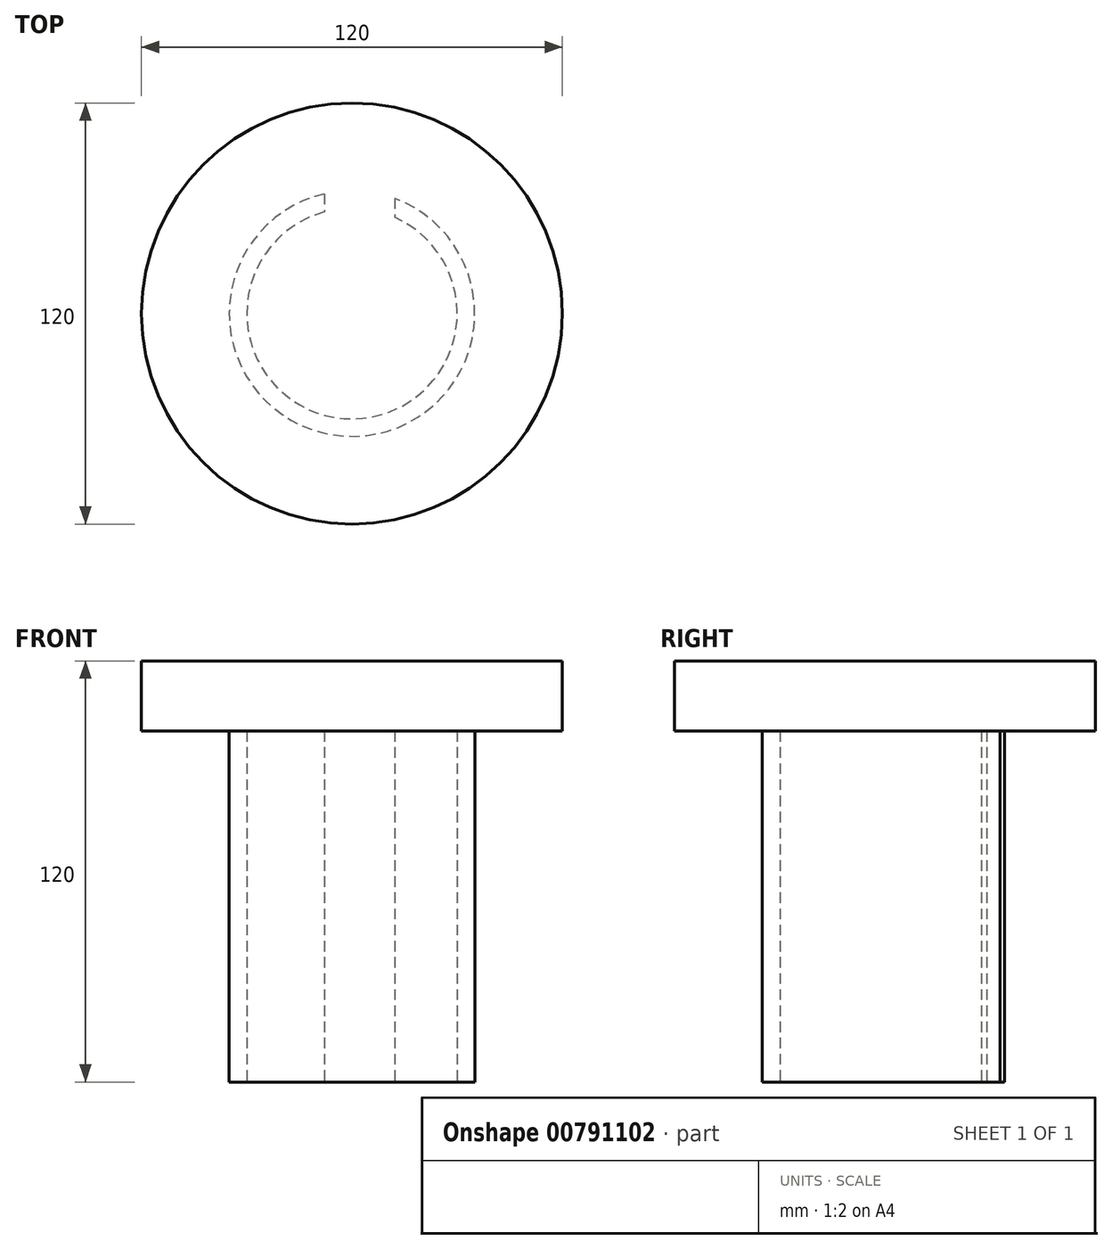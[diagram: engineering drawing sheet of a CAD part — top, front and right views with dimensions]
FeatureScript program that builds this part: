
annotation { "Feature Type Name" : "Feature", "Feature Type Description" : "" }
export const myFeature = defineFeature(function(context is Context, id is Id, definition is map)
    precondition{}
    {
        {
            var Q0;
            Q0=qCreatedBy(makeId("Top.planeOp"),FACE);
            var sketch = newSketch(context, id + "F0", { "sketchPlane" : qUnion([Q0])});
            skCircle(sketch, "E0", {"center": v(0, 0) * mm, "radius": 60 * mm});
            skSolve(sketch);
        }
        {
            var Q0;
            Q0=makeQuery(id+"F0.imprint","IMPRINT",FACE,{"disambiguationData":[TD([[makeQuery(id+"F0.imprint","IMPRINT",EDGE,{"derivedFrom":sQuery(id+"F0.wireOp",EDGE,"E0")}),1.0]])]});
            extrude(context, id + "F1", {"entities" : qUnion([Q0]), "depth" : 20 * mm, "offsetDistance" : 25.4 * mm});
        }
        {
            var Q0;
            Q0=makeQuery(id+"F1.opExtrude","CAP_FACE",FACE,{"disambiguationData":[OSD([sQuery(id+"F0.wireOp",EDGE,"E0")])],"isStart":true});
            var sketch = newSketch(context, id + "F2", { "sketchPlane" : qUnion([Q0])});
            skCircle(sketch, "E1", {"center": v(0, 0) * mm, "radius": 35 * mm});
            skSolve(sketch);
        }
        {
            var Q0;
            Q0 = qSketchRegion(id + "F2", true);
            extrude(context, id + "F3", {"entities" : qUnion([Q0]), "operationType" : NewBodyOperationType.ADD, "depth" : 100 * mm, "offsetDistance" : 25.4 * mm});
        }
        {
            var Q0;
            Q0=makeQuery(id+"F3.opExtrude","CAP_FACE",FACE,{"disambiguationData":[OSD([sQuery(id+"F2.wireOp",EDGE,"E1")])],"isStart":false});
            var sketch = newSketch(context, id + "F4", { "sketchPlane" : qUnion([Q0])});
            skCircle(sketch, "E2", {"center": v(0, 0) * mm, "radius": 30 * mm});
            skLineSegment(sketch, "E3.bottom", {"start": v(12.15, -40.92) * mm, "end": v(-7.85, -40.92) * mm});
            skLineSegment(sketch, "E3.top", {"start": v(12.15, -25.46) * mm, "end": v(-7.85, -25.46) * mm});
            skLineSegment(sketch, "E3.left", {"start": v(12.15, -40.92) * mm, "end": v(12.15, -25.46) * mm});
            skLineSegment(sketch, "E3.right", {"start": v(-7.85, -40.92) * mm, "end": v(-7.85, -25.46) * mm});
            skSolve(sketch);
        }
        {
            var Q0;
            {var subQ5=sQuery(id+"F4.wireOp",EDGE,"E3.top");Q0=makeQuery(id+"F4.imprint","IMPRINT",FACE,{"disambiguationData":[TD([[makeQuery(id+"F4.imprint","IMPRINT",EDGE,{"derivedFrom":subQ5}),1.0]])]});}
            var Q1;
            {var subQ5=sQuery(id+"F4.wireOp",EDGE,"E3.top");Q1=makeQuery(id+"F4.imprint","IMPRINT",FACE,{"disambiguationData":[TD([[makeQuery(id+"F4.imprint","IMPRINT",EDGE,{"derivedFrom":subQ5}),-1.0]])]});}
            var Q2;
            {var subQ0=sQuery(id+"F4.wireOp",EDGE,"E3.left");var subQ1=sQuery(id+"F4.wireOp",EDGE,"E2");var subQ2=makeQuery(id+"F4.imprint","INTERSECT",VERTEX,{"derivedFrom":[subQ1,subQ0]});Q2=makeQuery(id+"F4.imprint","IMPRINT",FACE,{"disambiguationData":[TD([[makeQuery(id+"F4.imprint","IMPRINT",EDGE,{"disambiguationData":[TD([[subQ2,1.0]])],"derivedFrom":subQ1}),-1.0]])]});}
            extrude(context, id + "F5", {"entities" : qUnion([Q0, Q1, Q2]), "operationType" : NewBodyOperationType.REMOVE, "oppositeDirection" : true, "depth" : 100 * mm, "offsetDistance" : 25.4 * mm});
        }
    });
